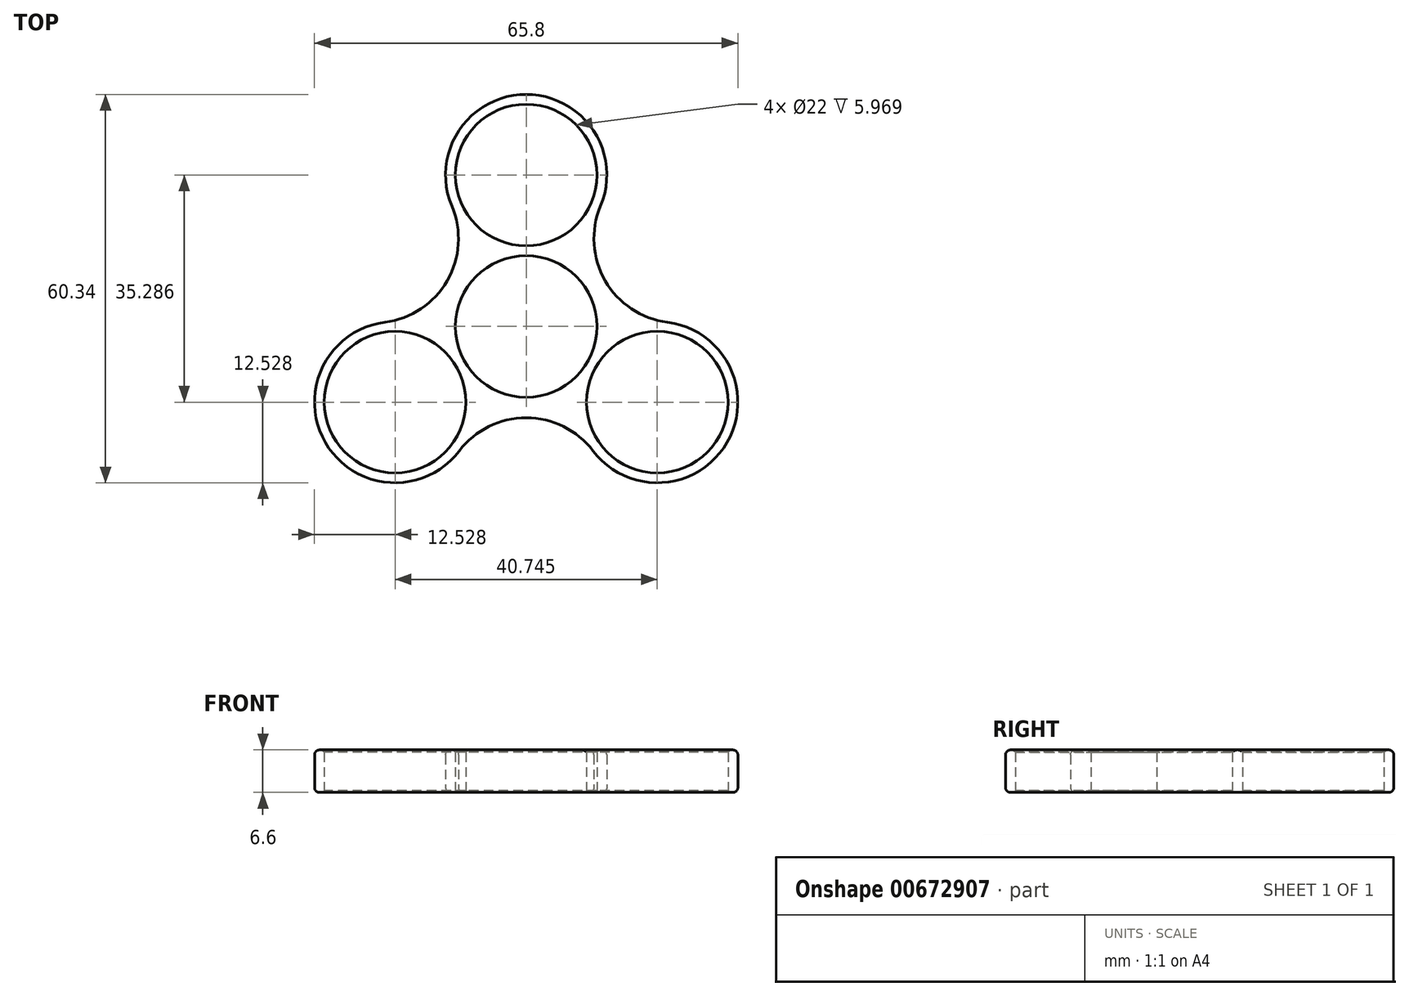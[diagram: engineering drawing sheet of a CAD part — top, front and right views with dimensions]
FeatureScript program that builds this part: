
annotation { "Feature Type Name" : "Feature", "Feature Type Description" : "" }
export const myFeature = defineFeature(function(context is Context, id is Id, definition is map)
    precondition{}
    {
        {
            var Q0;
            Q0=qCreatedBy(makeId("Top.planeOp"),FACE);
            var sketch = newSketch(context, id + "F0", { "sketchPlane" : qUnion([Q0])});
            skCircle(sketch, "E0", {"center": v(0, 0) * mm, "radius": 11 * mm});
            skArc(sketch, "E1.0", {"start": v(-4.3, 11.76) * mm, "mid": v(-10.85, 6.26) * mm, "end": v(-12.34, -2.16) * mm});
            skCircle(sketch, "E2", {"center": v(0, 23.52) * mm, "radius": 11 * mm});
            skCircle(sketch, "E3.0", {"center": v(0, 23.52) * mm, "radius": 12.52 * mm});
            skCircle(sketch, "E4.1.0", {"center": v(-20.37, -11.76) * mm, "radius": 11 * mm});
            skCircle(sketch, "E4.1.1", {"center": v(-20.37, -11.76) * mm, "radius": 12.52 * mm});
            skCircle(sketch, "E4.2.0", {"center": v(20.37, -11.76) * mm, "radius": 11 * mm});
            skCircle(sketch, "E4.2.1", {"center": v(20.37, -11.76) * mm, "radius": 12.52 * mm});
            skCircle(sketch, "E5", {"center": v(0, 0) * mm, "radius": 23.52 * mm, "construction": true});
            skArc(sketch, "E6.trimOffspring", {"start": v(12.34, -2.16) * mm, "mid": v(10.85, 6.26) * mm, "end": v(4.3, 11.76) * mm});
            skArc(sketch, "E7.trimOffspring", {"start": v(-8.04, -9.6) * mm, "mid": v(0, -12.52) * mm, "end": v(8.04, -9.6) * mm});
            skArc(sketch, "E8", {"start": v(11.55, 18.67) * mm, "mid": v(12.28, 7.09) * mm, "end": v(21.94, 0.66) * mm});
            skArc(sketch, "E9", {"start": v(-21.94, 0.66) * mm, "mid": v(-12.28, 7.09) * mm, "end": v(-11.55, 18.67) * mm});
            skArc(sketch, "E10", {"start": v(10.4, -19.34) * mm, "mid": v(0, -14.17) * mm, "end": v(-10.4, -19.34) * mm});
            skSolve(sketch);
        }
        {
            var Q0;
            Q0=makeQuery(id+"F0.imprint","IMPRINT",FACE,{"disambiguationData":[TD([[makeQuery(id+"F0.imprint","IMPRINT",EDGE,{"derivedFrom":sQuery(id+"F0.wireOp",EDGE,"E2")}),-1.0]])]});
            var Q1;
            {var subQ5=sQuery(id+"F0.wireOp",EDGE,"E1.0");Q1=makeQuery(id+"F0.imprint","IMPRINT",FACE,{"disambiguationData":[TD([[makeQuery(id+"F0.imprint","IMPRINT",EDGE,{"derivedFrom":subQ5}),1.0]])]});}
            var Q2;
            {var subQ5=sQuery(id+"F0.wireOp",EDGE,"E6.trimOffspring");Q2=makeQuery(id+"F0.imprint","IMPRINT",FACE,{"disambiguationData":[TD([[makeQuery(id+"F0.imprint","IMPRINT",EDGE,{"derivedFrom":subQ5}),1.0]])]});}
            var Q3;
            {var subQ5=sQuery(id+"F0.wireOp",EDGE,"E7.trimOffspring");Q3=makeQuery(id+"F0.imprint","IMPRINT",FACE,{"disambiguationData":[TD([[makeQuery(id+"F0.imprint","IMPRINT",EDGE,{"derivedFrom":subQ5}),1.0]])]});}
            var Q4;
            Q4=makeQuery(id+"F0.imprint","IMPRINT",FACE,{"disambiguationData":[TD([[makeQuery(id+"F0.imprint","IMPRINT",EDGE,{"derivedFrom":sQuery(id+"F0.wireOp",EDGE,"E4.2.0")}),-1.0]])]});
            var Q5;
            Q5=makeQuery(id+"F0.imprint","IMPRINT",FACE,{"disambiguationData":[TD([[makeQuery(id+"F0.imprint","IMPRINT",EDGE,{"derivedFrom":sQuery(id+"F0.wireOp",EDGE,"E4.1.0")}),-1.0]])]});
            var Q6;
            {var subQ0=sQuery(id+"F0.wireOp",EDGE,"E1.0");Q6=makeQuery(id+"F0.imprint","IMPRINT",FACE,{"disambiguationData":[TD([[makeQuery(id+"F0.imprint","IMPRINT",EDGE,{"derivedFrom":subQ0}),-1.0]])]});}
            var Q7;
            {var subQ0=sQuery(id+"F0.wireOp",EDGE,"E6.trimOffspring");Q7=makeQuery(id+"F0.imprint","IMPRINT",FACE,{"disambiguationData":[TD([[makeQuery(id+"F0.imprint","IMPRINT",EDGE,{"derivedFrom":subQ0}),-1.0]])]});}
            var Q8;
            {var subQ0=sQuery(id+"F0.wireOp",EDGE,"E7.trimOffspring");Q8=makeQuery(id+"F0.imprint","IMPRINT",FACE,{"disambiguationData":[TD([[makeQuery(id+"F0.imprint","IMPRINT",EDGE,{"derivedFrom":subQ0}),-1.0]])]});}
            extrude(context, id + "F1", {"entities" : qUnion([Q0, Q1, Q2, Q3, Q4, Q5, Q6, Q7, Q8]), "depth" : 6.35 * mm, "offsetDistance" : 25.4 * mm});
        }
        {
            var Q0;
            Q0=qCreatedBy(makeId("Top.planeOp"),FACE);
            var sketch = newSketch(context, id + "F2", { "sketchPlane" : qUnion([Q0])});
            skArc(sketch, "E11.0.0", {"start": v(11.55, 18.67) * mm, "mid": v(12.28, 7.09) * mm, "end": v(21.94, 0.66) * mm});
            skArc(sketch, "E11.0.1", {"start": v(21.94, 0.66) * mm, "mid": v(31.22, -18.02) * mm, "end": v(10.4, -19.34) * mm});
            skArc(sketch, "E11.0.2", {"start": v(10.4, -19.34) * mm, "mid": v(0, -14.17) * mm, "end": v(-10.4, -19.34) * mm});
            skArc(sketch, "E11.0.3", {"start": v(-10.4, -19.34) * mm, "mid": v(-31.22, -18.02) * mm, "end": v(-21.94, 0.66) * mm});
            skArc(sketch, "E11.0.4", {"start": v(-21.94, 0.66) * mm, "mid": v(-12.28, 7.09) * mm, "end": v(-11.55, 18.67) * mm});
            skArc(sketch, "E11.0.5", {"start": v(-11.55, 18.67) * mm, "mid": v(0, 36.05) * mm, "end": v(11.55, 18.67) * mm});
            skSolve(sketch);
        }
        {
            var Q0;
            Q0=makeQuery(id+"F2.imprint","IMPRINT",FACE,{"disambiguationData":[TD([[makeQuery(id+"F2.imprint","IMPRINT",EDGE,{"derivedFrom":sQuery(id+"F2.wireOp",EDGE,"E11.0.0")}),-1.0]])]});
            extrude(context, id + "F3", {"entities" : qUnion([Q0]), "operationType" : NewBodyOperationType.ADD, "oppositeDirection" : true, "depth" : 0.25 * mm, "offsetDistance" : 25.4 * mm});
        }
        {
            var Q0;
            Q0=makeQuery(id+"F1.opExtrude","CAP_EDGE",EDGE,{"disambiguationData":[OSD([sQuery(id+"F0.wireOp",EDGE,"E0")])],"isStart":false});
            var Q1;
            Q1=makeQuery(id+"F1.opExtrude","CAP_EDGE",EDGE,{"disambiguationData":[OSD([sQuery(id+"F0.wireOp",EDGE,"E4.2.0")])],"isStart":false});
            var Q2;
            Q2=makeQuery(id+"F1.opExtrude","CAP_EDGE",EDGE,{"disambiguationData":[OSD([sQuery(id+"F0.wireOp",EDGE,"E4.1.0")])],"isStart":false});
            var Q3;
            Q3=makeQuery(id+"F1.opExtrude","CAP_EDGE",EDGE,{"disambiguationData":[OSD([sQuery(id+"F0.wireOp",EDGE,"E2")])],"isStart":false});
            chamfer(context, id + "F4", {"entities" : qUnion([Q0, Q1, Q2, Q3]), "width" : 0.38 * mm, "tangentPropagation" : true});
        }
        {
            var Q0;
            Q0=makeQuery(id+"F1.opExtrude","CAP_FACE",FACE,{"disambiguationData":[OSD([sQuery(id+"F0.wireOp",EDGE,"E0"),sQuery(id+"F0.wireOp",EDGE,"E2"),sQuery(id+"F0.wireOp",EDGE,"E3.0"),sQuery(id+"F0.wireOp",EDGE,"E4.1.0"),sQuery(id+"F0.wireOp",EDGE,"E4.1.1"),sQuery(id+"F0.wireOp",EDGE,"E4.2.0"),sQuery(id+"F0.wireOp",EDGE,"E4.2.1"),sQuery(id+"F0.wireOp",EDGE,"E8"),sQuery(id+"F0.wireOp",EDGE,"E9"),sQuery(id+"F0.wireOp",EDGE,"E10")])],"isStart":false});
            fillet(context, id + "F5", {"entities" : qUnion([Q0]), "radius" : 0.76 * mm, "tangentPropagation" : true, "allowEdgeOverflow" : false});
        }
        {
            var Q0;
            Q0=makeQuery(id+"F3.opExtrude","CAP_FACE",FACE,{"disambiguationData":[OSD([sQuery(id+"F2.wireOp",EDGE,"E11.0.0"),sQuery(id+"F2.wireOp",EDGE,"E11.0.1"),sQuery(id+"F2.wireOp",EDGE,"E11.0.2"),sQuery(id+"F2.wireOp",EDGE,"E11.0.3"),sQuery(id+"F2.wireOp",EDGE,"E11.0.4"),sQuery(id+"F2.wireOp",EDGE,"E11.0.5")])],"isStart":false});
            fillet(context, id + "F6", {"entities" : qUnion([Q0]), "radius" : 0.76 * mm, "tangentPropagation" : true, "allowEdgeOverflow" : false});
        }
    });
